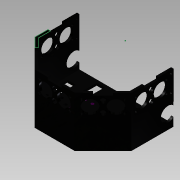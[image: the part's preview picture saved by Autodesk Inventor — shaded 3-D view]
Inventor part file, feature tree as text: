
AUTODESK INVENTOR PART (.ipt)
format: ipt  version: 2015 SP1 (Build 190203100, 203)  size: 464,384 bytes
history: native  units: mm
features: reference x56, sketch x20, extrude x20, projected_geometry x3
ambient origin geometry x8: Origin, YZ Plane, XZ Plane, XY Plane, X Axis, Y Axis, Z Axis, Center Point
bodies: Body1 (feature_tree)
feature tree (99):
  sketch  "Sketch1"  dims[d64=3.0mm d65=0.0mm d68=60.0mm d69=0.0mm]
  extrude  "Extrusion8"  Depth=60.0mm TaperAngle=0.0deg
  extrude  "Extrusion9"  Depth=3.5mm
  extrude  "Extrusion10"  Depth=3.5mm
  extrude  "Extrusion11"  Depth=3.5mm
  extrude  "Extrusion12"  Depth=10.0mm
  extrude  "Extrusion19"  Depth=17.5mm
  extrude  "Extrusion22"  Depth=17.5mm
  extrude  "Extrusion23"  Depth=10.0mm
  sketch  "Sketch22"  dims[d141=10.0mm d144=1.65mm]
  extrude  "Extrusion27"  Depth=10.0mm TaperAngle=0.0deg
  extrude  "Extrusion30"  Depth=3.5mm
  extrude  "Extrusion31"  Depth=7.0mm
  extrude  "Extrusion32"  Depth=7.0mm
  extrude  "Extrusion33"  Depth=10.0mm TaperAngle=0.0deg
  extrude  "Extrusion36"  Depth=17.5mm
  extrude  "Extrusion40"  Depth=3.0mm TaperAngle=0.0deg
  extrude  "Extrusion41"  Depth=120.811657mm
  extrude  "Extrusion42"  Depth=50.041827mm
  extrude  "Extrusion43"  Depth=52.663858mm
  extrude  "Extrusion44"  Depth=3.0mm
  extrude  "Extrusion45"  Depth=10.0mm
  sketch  "Sketch41"  dims[d206=47.556546mm d207=47.556546mm d208=47.556546mm d209=51.421217mm d210=135.0deg d211=135.0deg d212=135.0deg d213=135.0deg d214=135.0deg d215=135.0deg d216=135.0deg d217=135.0deg d218=3.0mm d219=3.0mm d220=3.0mm d221=3.0mm d222=0.0mm d223=17.500137mm d225=3.0mm d231=0.0mm d232=3.0mm d233=0.0mm d234=3.0mm d235=0.0mm d236=3.0mm d237=0.0mm d242=3.5mm d243=3.5mm d244=10.0mm d245=0.0mm d252=10.0mm d253=0.0mm d254=10.0mm d255=0.0mm d256=180.0mm d257=0.0mm d258=180.0mm d259=0.0mm d260=180.0mm d261=0.0mm d262=3.5mm d263=3.5mm d264=3.5mm d265=3.5mm d266=10.0mm d267=0.0mm]
  sketch  "Sketch10"  dims[d115=3.5mm d116=3.5mm]
  sketch  "Sketch11"  dims[d117=3.5mm d118=3.5mm]
  reference  "Reference28"
  reference  "Reference29"
  reference  "Reference30"
  reference  "Reference31"
  reference  "Reference32"
  reference  "Reference33"
  reference  "Reference34"
  sketch  "Sketch12"  dims[d119=3.5mm d120=3.5mm]
  reference  "Reference35"
  reference  "Reference36"
  sketch  "Sketch18"  dims[d127=10.0mm d128=0.0mm d129=10.0mm]
  sketch  "Sketch20"  dims[d130=17.5mm d132=17.5mm]
  reference  "Reference75"
  reference  "Reference76"
  sketch  "Sketch21"  dims[d133=15.0mm d136=17.5mm d137=10.0mm]
  sketch  "Sketch23"  dims[d145=10.0mm d146=0.0mm d147=10.0mm d148=0.0mm]
  reference  "Reference79"
  reference  "Reference80"
  reference  "Reference81"
  reference  "Reference82"
  sketch  "Sketch26"  dims[d161=3.5mm d162=3.5mm]
  reference  "Reference83"
  reference  "Reference84"
  reference  "Reference85"
  reference  "Reference86"
  reference  "Reference87"
  reference  "Reference88"
  reference  "Reference89"
  reference  "Reference90"
  projected_geometry  "Projected Loop2"
  sketch  "Sketch27"  dims[d163=7.0mm d164=7.0mm]
  sketch  "Sketch28"  dims[d165=7.0mm d166=7.0mm]
  projected_geometry  "Projected Loop3"
  sketch  "Sketch31"  dims[d167=10.0mm d168=0.0mm d173=10.0mm d174=0.0mm]
  sketch  "Sketch34"  dims[d175=10.0mm d176=0.0mm d181=17.5mm]
  reference  "Reference97"
  reference  "Reference98"
  reference  "Reference99"
  reference  "Reference100"
  reference  "Reference101"
  reference  "Reference102"
  reference  "Reference103"
  reference  "Reference104"
  sketch  "Sketch35"  dims[d186=10.0mm d187=0.0mm d193=3.0mm d194=0.0mm]
  reference  "Reference105"
  reference  "Reference106"
  reference  "Reference107"
  reference  "Reference108"
  reference  "Reference109"
  reference  "Reference110"
  reference  "Reference111"
  reference  "Reference112"
  sketch  "Sketch36"  dims[d195=120.811657mm d198=50.041827mm]
  reference  "Reference113"
  reference  "Reference114"
  reference  "Reference115"
  reference  "Reference116"
  reference  "Reference117"
  reference  "Reference118"
  reference  "Reference119"
  reference  "Reference120"
  sketch  "Sketch37"  dims[d199=50.041827mm d200=50.041827mm]
  reference  "Reference121"
  reference  "Reference122"
  reference  "Reference123"
  reference  "Reference124"
  reference  "Reference125"
  reference  "Reference126"
  reference  "Reference127"
  reference  "Reference128"
  sketch  "Sketch38"  dims[d201=52.663858mm d202=52.663858mm]
  reference  "Reference129"
  sketch  "Sketch40"  dims[d204=3.0mm d205=51.421217mm]
  projected_geometry  "Projected Loop5"
